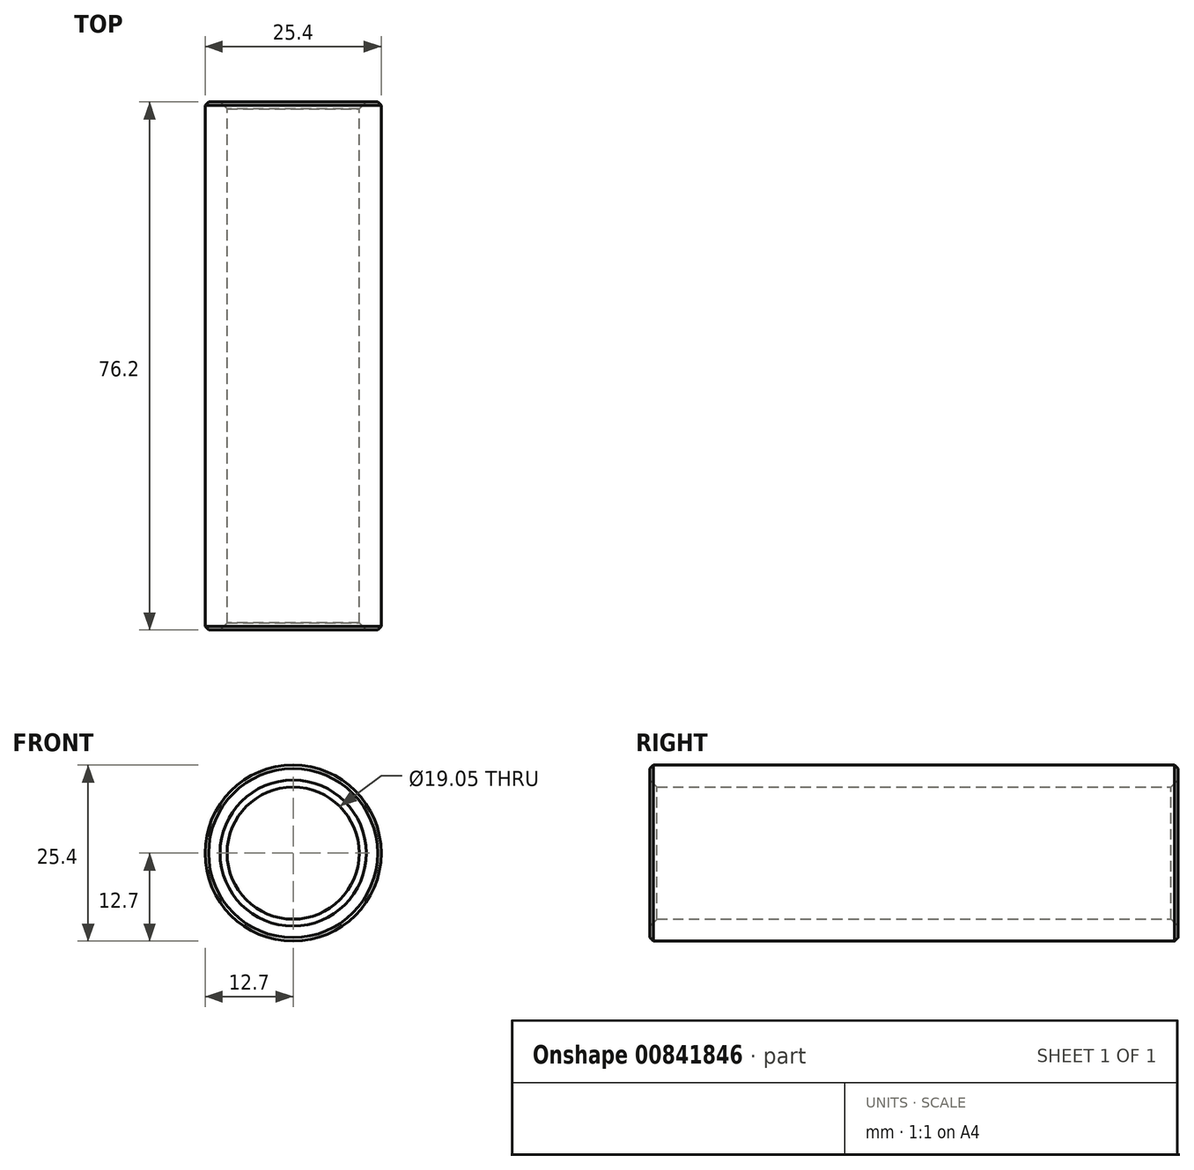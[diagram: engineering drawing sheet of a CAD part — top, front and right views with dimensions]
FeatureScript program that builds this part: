
annotation { "Feature Type Name" : "Feature", "Feature Type Description" : "" }
export const myFeature = defineFeature(function(context is Context, id is Id, definition is map)
    precondition{}
    {
        {
            var Q0;
            Q0=qCreatedBy(makeId("Front.planeOp"),FACE);
            var sketch = newSketch(context, id + "F0", { "sketchPlane" : qUnion([Q0])});
            skCircle(sketch, "E0", {"center": v(0, 0) * mm, "radius": 9.53 * mm});
            skCircle(sketch, "E1", {"center": v(0, 0) * mm, "radius": 12.7 * mm});
            skSolve(sketch);
        }
        {
            var Q0;
            Q0 = qSketchRegion(id + "F0", true);
            extrude(context, id + "F1", {"entities" : qUnion([Q0]), "depth" : 38.1 * mm, "offsetDistance" : 25.4 * mm, "hasSecondDirection" : true, "secondDirectionOppositeDirection" : true, "secondDirectionDepth" : 38.1 * mm});
        }
        {
            var Q0;
            Q0=makeQuery(id+"F1.opExtrude","CAP_EDGE",EDGE,{"disambiguationData":[OSD([sQuery(id+"F0.wireOp",EDGE,"E0")])],"isStart":false});
            var Q1;
            Q1=makeQuery(id+"F1.opExtrude","CAP_EDGE",EDGE,{"disambiguationData":[OSD([sQuery(id+"F0.wireOp",EDGE,"E0")])],"isStart":true});
            chamfer(context, id + "F2", {"entities" : qUnion([Q0, Q1]), "width" : 1.02 * mm, "tangentPropagation" : true});
        }
        {
            var Q0;
            Q0=makeQuery(id+"F1.opExtrude","CAP_EDGE",EDGE,{"disambiguationData":[OSD([sQuery(id+"F0.wireOp",EDGE,"E1")])],"isStart":true});
            var Q1;
            Q1=makeQuery(id+"F1.opExtrude","CAP_EDGE",EDGE,{"disambiguationData":[OSD([sQuery(id+"F0.wireOp",EDGE,"E1")])],"isStart":false});
            chamfer(context, id + "F3", {"entities" : qUnion([Q0, Q1]), "width" : 0.5 * mm, "tangentPropagation" : true});
        }
    });
